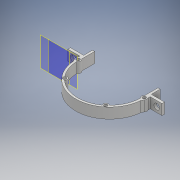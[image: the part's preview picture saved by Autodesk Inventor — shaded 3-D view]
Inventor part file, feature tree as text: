
AUTODESK INVENTOR PART (.ipt)
format: ipt  version: 2017 (Build 210142000, 142)  size: 178,176 bytes
history: native  units: mm
features: sketch x2, other x2, extrude x2, projected_geometry x2
ambient origin geometry x8: Origin, YZ Plane, XZ Plane, XY Plane, X Axis, Y Axis, Z Axis, Center Point
bodies: Body1 (feature_tree)
feature tree (8):
  sketch  "Esquisse1"
  other  "Plan de construction1"
  other  "Plan de construction2"
  sketch  "Esquisse3"
  extrude  "Extrusion16"  Depth=2.0mm
  extrude  "Extrusion17"  Depth=2.0mm
  projected_geometry  "Boucle projetée3"
  projected_geometry  "Boucle projetée4"
